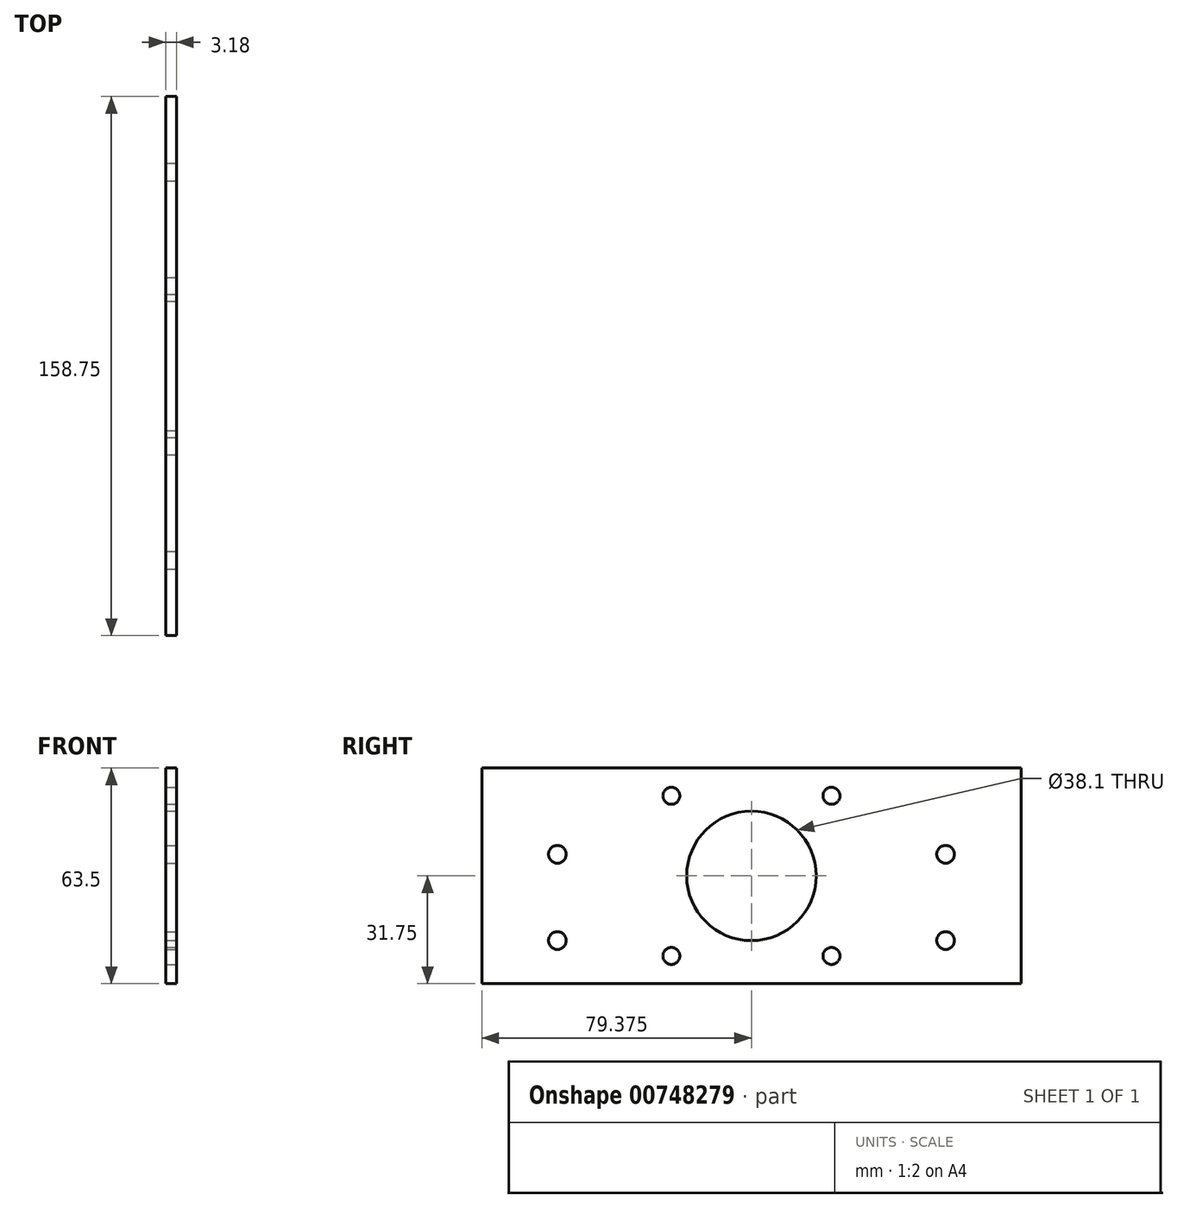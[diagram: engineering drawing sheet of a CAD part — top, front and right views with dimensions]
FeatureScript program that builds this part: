
annotation { "Feature Type Name" : "Feature", "Feature Type Description" : "" }
export const myFeature = defineFeature(function(context is Context, id is Id, definition is map)
    precondition{}
    {
        {
            var Q0;
            Q0=qCreatedBy(makeId("Front.planeOp"),FACE);
            var sketch = newSketch(context, id + "F0", { "sketchPlane" : qUnion([Q0])});
            skLineSegment(sketch, "E0.bottom", {"start": v(1.59, -31.75) * mm, "end": v(-1.59, -31.75) * mm});
            skLineSegment(sketch, "E0.top", {"start": v(1.59, 31.75) * mm, "end": v(-1.59, 31.75) * mm});
            skLineSegment(sketch, "E0.left", {"start": v(1.59, -31.75) * mm, "end": v(1.59, 31.75) * mm});
            skLineSegment(sketch, "E0.right", {"start": v(-1.59, -31.75) * mm, "end": v(-1.59, 31.75) * mm});
            skPoint(sketch, "E0.middle", {"position": v(0, 0) * mm});
            skSolve(sketch);
        }
        {
            var Q0;
            Q0=qSketchRegion(id+"F0",true);
            extrude(context, id + "F1", {"entities" : qUnion([Q0]), "depth" : 158.75 * mm, "offsetDistance" : 25.4 * mm});
        }
        {
            var Q0;
            Q0=makeQuery(id+"F1.opExtrude","SWEPT_FACE",FACE,{"disambiguationData":[OSD([sQuery(id+"F0.wireOp",EDGE,"E0.left")])]});
            var sketch = newSketch(context, id + "F2", { "sketchPlane" : qUnion([Q0])});
            skLineSegment(sketch, "E1", {"start": v(-79.38, 31.75) * mm, "end": v(-79.38, -31.75) * mm, "construction": true});
            skLineSegment(sketch, "E2", {"start": v(-158.75, 0) * mm, "end": v(0, 0) * mm, "construction": true});
            skLineSegment(sketch, "E3.bottom", {"start": v(-55.8, -23.57) * mm, "end": v(-102.95, -23.57) * mm, "construction": true});
            skLineSegment(sketch, "E3.top", {"start": v(-55.8, 23.57) * mm, "end": v(-102.95, 23.57) * mm, "construction": true});
            skLineSegment(sketch, "E3.left", {"start": v(-55.8, -23.57) * mm, "end": v(-55.8, 23.57) * mm, "construction": true});
            skLineSegment(sketch, "E3.right", {"start": v(-102.95, -23.57) * mm, "end": v(-102.95, 23.57) * mm, "construction": true});
            skPoint(sketch, "E3.middle", {"position": v(-79.38, 0) * mm});
            skCircle(sketch, "E4", {"center": v(-102.95, 23.57) * mm, "radius": 2.5 * mm});
            skCircle(sketch, "E5", {"center": v(-55.8, 23.57) * mm, "radius": 2.5 * mm});
            skCircle(sketch, "E6", {"center": v(-102.95, -23.57) * mm, "radius": 2.5 * mm});
            skCircle(sketch, "E7", {"center": v(-55.8, -23.57) * mm, "radius": 2.5 * mm});
            skCircle(sketch, "E8", {"center": v(-79.38, 0) * mm, "radius": 19.05 * mm});
            skLineSegment(sketch, "E9", {"start": v(-136.53, 31.75) * mm, "end": v(-136.53, -31.75) * mm, "construction": true});
            skLineSegment(sketch, "E10", {"start": v(-22.23, 31.75) * mm, "end": v(-22.23, -31.75) * mm, "construction": true});
            skLineSegment(sketch, "E11", {"start": v(-158.75, 6.35) * mm, "end": v(0, 6.35) * mm, "construction": true});
            skLineSegment(sketch, "E12", {"start": v(-158.75, -19.05) * mm, "end": v(0, -19.05) * mm, "construction": true});
            skCircle(sketch, "E13", {"center": v(-22.23, 6.35) * mm, "radius": 2.62 * mm});
            skCircle(sketch, "E14", {"center": v(-22.23, -19.05) * mm, "radius": 2.62 * mm});
            skCircle(sketch, "E15", {"center": v(-136.53, 6.35) * mm, "radius": 2.62 * mm});
            skCircle(sketch, "E16", {"center": v(-136.53, -19.05) * mm, "radius": 2.62 * mm});
            skSolve(sketch);
        }
        {
            var Q0;
            Q0=qSketchRegion(id+"F2",true);
            extrude(context, id + "F3", {"entities" : qUnion([Q0]), "operationType" : NewBodyOperationType.REMOVE, "endBound" : BoundingType.THROUGH_ALL, "oppositeDirection" : true, "depth" : 25.4 * mm, "offsetDistance" : 25.4 * mm});
        }
    });
